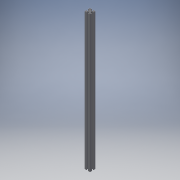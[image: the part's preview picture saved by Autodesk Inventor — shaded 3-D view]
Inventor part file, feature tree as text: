
AUTODESK INVENTOR PART (.ipt)
format: ipt  version: 2019 (Build 230136000, 136)  size: 186,368 bytes
history: native  units: mm
features: other x1, extrude x1, sketch x1
ambient origin geometry x8: Origin, YZ Plane, XZ Plane, XY Plane, X Axis, Y Axis, Z Axis, Center Point
bodies: Body1 (feature_tree)
feature tree (3):
  other  "솔리드1"
  extrude  "돌출1"  Depth=20.0mm
  sketch  "스케치1"
